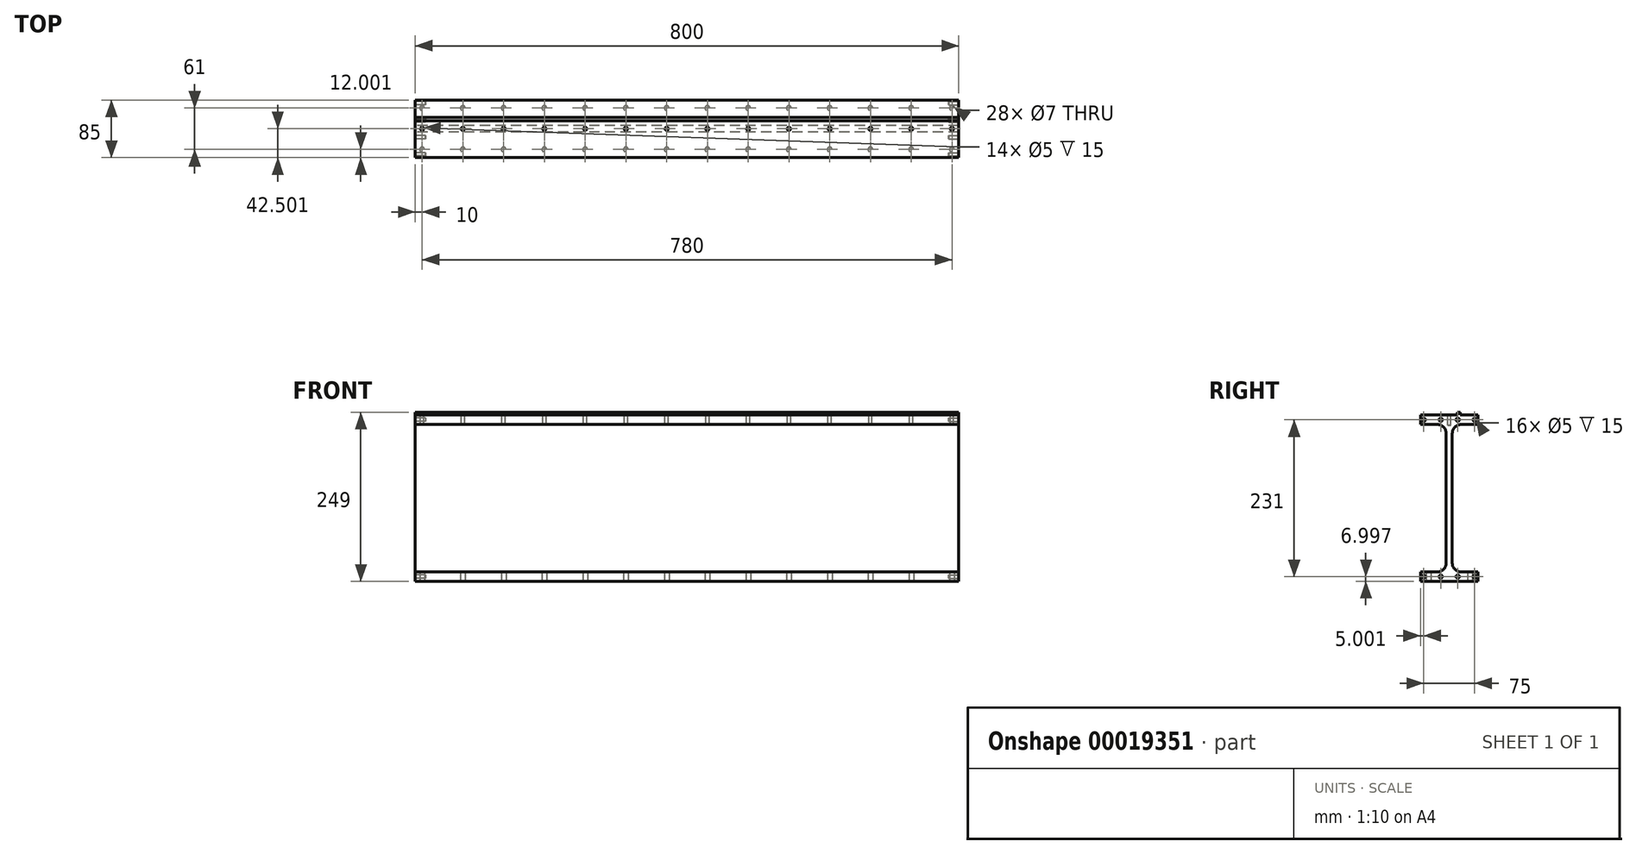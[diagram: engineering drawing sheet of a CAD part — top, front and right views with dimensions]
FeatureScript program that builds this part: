
annotation { "Feature Type Name" : "Feature", "Feature Type Description" : "" }
export const myFeature = defineFeature(function(context is Context, id is Id, definition is map)
    precondition{}
    {
        {
            var Q0;
            Q0=qCreatedBy(makeId("Right.planeOp"),FACE);
            var sketch = newSketch(context, id + "F0", { "sketchPlane" : qUnion([Q0])});
            skLineSegment(sketch, "E0", {"start": v(-399.15, 62.6) * mm, "end": v(-484.15, 62.6) * mm});
            skLineSegment(sketch, "E1", {"start": v(-484.15, 62.6) * mm, "end": v(-484.15, 48.6) * mm});
            skLineSegment(sketch, "E2", {"start": v(-484.15, 48.6) * mm, "end": v(-459.15, 48.6) * mm});
            skLineSegment(sketch, "E3", {"start": v(-446.15, 35.6) * mm, "end": v(-446.15, -155.4) * mm});
            skLineSegment(sketch, "E4", {"start": v(-459.15, -168.4) * mm, "end": v(-484.15, -168.4) * mm});
            skLineSegment(sketch, "E5", {"start": v(-484.15, -168.4) * mm, "end": v(-484.15, -182.4) * mm});
            skLineSegment(sketch, "E6", {"start": v(-484.15, -182.4) * mm, "end": v(-399.15, -182.4) * mm});
            skLineSegment(sketch, "E7", {"start": v(-399.15, -182.4) * mm, "end": v(-399.15, -168.4) * mm});
            skLineSegment(sketch, "E8", {"start": v(-399.15, -168.4) * mm, "end": v(-424.15, -168.4) * mm});
            skLineSegment(sketch, "E9", {"start": v(-437.15, -155.4) * mm, "end": v(-437.15, 35.6) * mm});
            skLineSegment(sketch, "E10", {"start": v(-424.15, 48.6) * mm, "end": v(-399.15, 48.6) * mm});
            skLineSegment(sketch, "E11", {"start": v(-399.15, 48.6) * mm, "end": v(-399.15, 62.6) * mm});
            skArc(sketch, "E12.filletArc", {"start": v(-446.15, 35.6) * mm, "mid": v(-449.96, 44.8) * mm, "end": v(-459.15, 48.6) * mm});
            skArc(sketch, "E13.filletArc", {"start": v(-424.15, 48.6) * mm, "mid": v(-433.34, 44.8) * mm, "end": v(-437.15, 35.6) * mm});
            skArc(sketch, "E14.filletArc", {"start": v(-437.15, -155.4) * mm, "mid": v(-433.34, -164.59) * mm, "end": v(-424.15, -168.4) * mm});
            skArc(sketch, "E15.filletArc", {"start": v(-459.15, -168.4) * mm, "mid": v(-449.96, -164.59) * mm, "end": v(-446.15, -155.4) * mm});
            skSolve(sketch);
        }
        {
            var Q0;
            Q0=makeQuery(id+"F0.imprint","IMPRINT",FACE,{"disambiguationData":[TD([[makeQuery(id+"F0.imprint","IMPRINT",EDGE,{"derivedFrom":sQuery(id+"F0.wireOp",EDGE,"E0")}),1.0]])]});
            extrude(context, id + "F1", {"entities" : qUnion([Q0]), "depth" : 800 * mm});
        }
        {
            var Q0;
            Q0=makeQuery(id+"F1.opExtrude","SWEPT_FACE",FACE,{"disambiguationData":[OSD([sQuery(id+"F0.wireOp",EDGE,"E0")])]});
            var sketch = newSketch(context, id + "F2", { "sketchPlane" : qUnion([Q0])});
            skCircle(sketch, "E16", {"center": v(190, -441.65) * mm, "radius": 2.5 * mm});
            skCircle(sketch, "E17", {"center": v(250, -441.65) * mm, "radius": 2.5 * mm});
            skCircle(sketch, "E18", {"center": v(310, -441.65) * mm, "radius": 2.5 * mm});
            skCircle(sketch, "E19", {"center": v(370, -441.65) * mm, "radius": 2.5 * mm});
            skCircle(sketch, "E20", {"center": v(430, -441.65) * mm, "radius": 2.5 * mm});
            skCircle(sketch, "E21", {"center": v(490, -441.65) * mm, "radius": 2.5 * mm});
            skCircle(sketch, "E22", {"center": v(550, -441.65) * mm, "radius": 2.5 * mm});
            skCircle(sketch, "E23", {"center": v(610, -441.65) * mm, "radius": 2.5 * mm});
            skCircle(sketch, "E24", {"center": v(670, -441.65) * mm, "radius": 2.5 * mm});
            skCircle(sketch, "E25", {"center": v(10, -441.65) * mm, "radius": 2.5 * mm});
            skCircle(sketch, "E26", {"center": v(70, -441.65) * mm, "radius": 2.5 * mm});
            skCircle(sketch, "E27", {"center": v(130, -441.65) * mm, "radius": 2.5 * mm});
            skCircle(sketch, "E28", {"center": v(730, -441.65) * mm, "radius": 2.5 * mm});
            skCircle(sketch, "E29", {"center": v(790, -441.65) * mm, "radius": 2.5 * mm});
            skPoint(sketch, "E30", {"position": v(0, -441.65) * mm});
            skLineSegment(sketch, "E31.bottom", {"start": v(0, -425.15) * mm, "end": v(800, -425.15) * mm});
            skLineSegment(sketch, "E31.top", {"start": v(0, -430.15) * mm, "end": v(800, -430.15) * mm});
            skLineSegment(sketch, "E31.left", {"start": v(0, -425.15) * mm, "end": v(0, -430.15) * mm});
            skLineSegment(sketch, "E31.right", {"start": v(800, -425.15) * mm, "end": v(800, -430.15) * mm});
            skSolve(sketch);
        }
        {
            var Q0;
            Q0=makeQuery(id+"F2.imprint","IMPRINT",FACE,{"disambiguationData":[TD([[makeQuery(id+"F2.imprint","IMPRINT",EDGE,{"derivedFrom":sQuery(id+"F2.wireOp",EDGE,"E25")}),1.0]])]});
            var Q1;
            Q1=makeQuery(id+"F2.imprint","IMPRINT",FACE,{"disambiguationData":[TD([[makeQuery(id+"F2.imprint","IMPRINT",EDGE,{"derivedFrom":sQuery(id+"F2.wireOp",EDGE,"E26")}),1.0]])]});
            var Q2;
            Q2=makeQuery(id+"F2.imprint","IMPRINT",FACE,{"disambiguationData":[TD([[makeQuery(id+"F2.imprint","IMPRINT",EDGE,{"derivedFrom":sQuery(id+"F2.wireOp",EDGE,"E27")}),1.0]])]});
            var Q3;
            Q3=makeQuery(id+"F2.imprint","IMPRINT",FACE,{"disambiguationData":[TD([[makeQuery(id+"F2.imprint","IMPRINT",EDGE,{"derivedFrom":sQuery(id+"F2.wireOp",EDGE,"E16")}),1.0]])]});
            var Q4;
            Q4=makeQuery(id+"F2.imprint","IMPRINT",FACE,{"disambiguationData":[TD([[makeQuery(id+"F2.imprint","IMPRINT",EDGE,{"derivedFrom":sQuery(id+"F2.wireOp",EDGE,"E17")}),1.0]])]});
            var Q5;
            Q5=makeQuery(id+"F2.imprint","IMPRINT",FACE,{"disambiguationData":[TD([[makeQuery(id+"F2.imprint","IMPRINT",EDGE,{"derivedFrom":sQuery(id+"F2.wireOp",EDGE,"E18")}),1.0]])]});
            var Q6;
            Q6=makeQuery(id+"F2.imprint","IMPRINT",FACE,{"disambiguationData":[TD([[makeQuery(id+"F2.imprint","IMPRINT",EDGE,{"derivedFrom":sQuery(id+"F2.wireOp",EDGE,"E19")}),1.0]])]});
            var Q7;
            Q7=makeQuery(id+"F2.imprint","IMPRINT",FACE,{"disambiguationData":[TD([[makeQuery(id+"F2.imprint","IMPRINT",EDGE,{"derivedFrom":sQuery(id+"F2.wireOp",EDGE,"E20")}),1.0]])]});
            var Q8;
            Q8=makeQuery(id+"F2.imprint","IMPRINT",FACE,{"disambiguationData":[TD([[makeQuery(id+"F2.imprint","IMPRINT",EDGE,{"derivedFrom":sQuery(id+"F2.wireOp",EDGE,"E21")}),1.0]])]});
            var Q9;
            Q9=makeQuery(id+"F2.imprint","IMPRINT",FACE,{"disambiguationData":[TD([[makeQuery(id+"F2.imprint","IMPRINT",EDGE,{"derivedFrom":sQuery(id+"F2.wireOp",EDGE,"E22")}),1.0]])]});
            var Q10;
            Q10=makeQuery(id+"F2.imprint","IMPRINT",FACE,{"disambiguationData":[TD([[makeQuery(id+"F2.imprint","IMPRINT",EDGE,{"derivedFrom":sQuery(id+"F2.wireOp",EDGE,"E23")}),1.0]])]});
            var Q11;
            Q11=makeQuery(id+"F2.imprint","IMPRINT",FACE,{"disambiguationData":[TD([[makeQuery(id+"F2.imprint","IMPRINT",EDGE,{"derivedFrom":sQuery(id+"F2.wireOp",EDGE,"E24")}),1.0]])]});
            var Q12;
            Q12=makeQuery(id+"F2.imprint","IMPRINT",FACE,{"disambiguationData":[TD([[makeQuery(id+"F2.imprint","IMPRINT",EDGE,{"derivedFrom":sQuery(id+"F2.wireOp",EDGE,"E28")}),1.0]])]});
            var Q13;
            Q13=makeQuery(id+"F2.imprint","IMPRINT",FACE,{"disambiguationData":[TD([[makeQuery(id+"F2.imprint","IMPRINT",EDGE,{"derivedFrom":sQuery(id+"F2.wireOp",EDGE,"E29")}),1.0]])]});
            extrude(context, id + "F3", {"entities" : qUnion([Q0, Q1, Q2, Q3, Q4, Q5, Q6, Q7, Q8, Q9, Q10, Q11, Q12, Q13]), "operationType" : NewBodyOperationType.REMOVE, "oppositeDirection" : true, "depth" : 15 * mm});
        }
        {
            var Q0;
            Q0=makeQuery(id+"F2.imprint","IMPRINT",FACE,{"disambiguationData":[TD([[makeQuery(id+"F2.imprint","IMPRINT",EDGE,{"derivedFrom":sQuery(id+"F2.wireOp",EDGE,"E31.bottom")}),-1.0]])]});
            extrude(context, id + "F4", {"entities" : qUnion([Q0]), "operationType" : NewBodyOperationType.ADD, "depth" : 4 * mm});
        }
        {
            var Q0;
            Q0=makeQuery(id+"F4.boolean.opBoolean","MERGE",FACE,{"derivedFrom":[makeQuery(id+"F1.opExtrude","CAP_FACE",FACE,{"disambiguationData":[OSD([sQuery(id+"F0.wireOp",EDGE,"E0"),sQuery(id+"F0.wireOp",EDGE,"E1"),sQuery(id+"F0.wireOp",EDGE,"E2"),sQuery(id+"F0.wireOp",EDGE,"E3"),sQuery(id+"F0.wireOp",EDGE,"E4"),sQuery(id+"F0.wireOp",EDGE,"E5"),sQuery(id+"F0.wireOp",EDGE,"E6"),sQuery(id+"F0.wireOp",EDGE,"E7"),sQuery(id+"F0.wireOp",EDGE,"E8"),sQuery(id+"F0.wireOp",EDGE,"E9"),sQuery(id+"F0.wireOp",EDGE,"E10"),sQuery(id+"F0.wireOp",EDGE,"E11"),sQuery(id+"F0.wireOp",EDGE,"E12.filletArc"),sQuery(id+"F0.wireOp",EDGE,"E13.filletArc"),sQuery(id+"F0.wireOp",EDGE,"E14.filletArc"),sQuery(id+"F0.wireOp",EDGE,"E15.filletArc")])],"isStart":true}),makeQuery(id+"F4.opExtrude","SWEPT_FACE",FACE,{"disambiguationData":[OSD([sQuery(id+"F2.wireOp",EDGE,"E31.left")])]})]});
            var sketch = newSketch(context, id + "F5", { "sketchPlane" : qUnion([Q0])});
            skPoint(sketch, "E32", {"position": v(399.15, 55.6) * mm});
            skCircle(sketch, "E33", {"center": v(404.15, 55.6) * mm, "radius": 2.5 * mm});
            skCircle(sketch, "E34", {"center": v(429.15, 55.6) * mm, "radius": 2.5 * mm});
            skCircle(sketch, "E35", {"center": v(454.15, 55.6) * mm, "radius": 2.5 * mm});
            skCircle(sketch, "E36", {"center": v(479.15, 55.6) * mm, "radius": 2.5 * mm});
            skCircle(sketch, "E37", {"center": v(404.15, -175.4) * mm, "radius": 2.5 * mm});
            skCircle(sketch, "E38", {"center": v(429.15, -175.4) * mm, "radius": 2.5 * mm});
            skCircle(sketch, "E39", {"center": v(454.15, -175.4) * mm, "radius": 2.5 * mm});
            skCircle(sketch, "E40", {"center": v(479.15, -175.4) * mm, "radius": 2.5 * mm});
            skPoint(sketch, "E41", {"position": v(399.15, -175.4) * mm});
            skSolve(sketch);
        }
        {
            var Q0;
            Q0=makeQuery(id+"F5.imprint","IMPRINT",FACE,{"disambiguationData":[TD([[makeQuery(id+"F5.imprint","IMPRINT",EDGE,{"derivedFrom":sQuery(id+"F5.wireOp",EDGE,"E33")}),1.0]])]});
            var Q1;
            Q1=makeQuery(id+"F5.imprint","IMPRINT",FACE,{"disambiguationData":[TD([[makeQuery(id+"F5.imprint","IMPRINT",EDGE,{"derivedFrom":sQuery(id+"F5.wireOp",EDGE,"E34")}),1.0]])]});
            var Q2;
            Q2=makeQuery(id+"F5.imprint","IMPRINT",FACE,{"disambiguationData":[TD([[makeQuery(id+"F5.imprint","IMPRINT",EDGE,{"derivedFrom":sQuery(id+"F5.wireOp",EDGE,"E35")}),1.0]])]});
            var Q3;
            Q3=makeQuery(id+"F5.imprint","IMPRINT",FACE,{"disambiguationData":[TD([[makeQuery(id+"F5.imprint","IMPRINT",EDGE,{"derivedFrom":sQuery(id+"F5.wireOp",EDGE,"E36")}),1.0]])]});
            var Q4;
            Q4=makeQuery(id+"F5.imprint","IMPRINT",FACE,{"disambiguationData":[TD([[makeQuery(id+"F5.imprint","IMPRINT",EDGE,{"derivedFrom":sQuery(id+"F5.wireOp",EDGE,"E37")}),1.0]])]});
            var Q5;
            Q5=makeQuery(id+"F5.imprint","IMPRINT",FACE,{"disambiguationData":[TD([[makeQuery(id+"F5.imprint","IMPRINT",EDGE,{"derivedFrom":sQuery(id+"F5.wireOp",EDGE,"E38")}),1.0]])]});
            var Q6;
            Q6=makeQuery(id+"F5.imprint","IMPRINT",FACE,{"disambiguationData":[TD([[makeQuery(id+"F5.imprint","IMPRINT",EDGE,{"derivedFrom":sQuery(id+"F5.wireOp",EDGE,"E39")}),1.0]])]});
            var Q7;
            Q7=makeQuery(id+"F5.imprint","IMPRINT",FACE,{"disambiguationData":[TD([[makeQuery(id+"F5.imprint","IMPRINT",EDGE,{"derivedFrom":sQuery(id+"F5.wireOp",EDGE,"E40")}),1.0]])]});
            extrude(context, id + "F6", {"entities" : qUnion([Q0, Q1, Q2, Q3, Q4, Q5, Q6, Q7]), "operationType" : NewBodyOperationType.REMOVE, "oppositeDirection" : true, "depth" : 15 * mm});
        }
        {
            var Q0;
            Q0=makeQuery(id+"F4.boolean.opBoolean","MERGE",FACE,{"derivedFrom":[makeQuery(id+"F1.opExtrude","CAP_FACE",FACE,{"disambiguationData":[OSD([sQuery(id+"F0.wireOp",EDGE,"E0"),sQuery(id+"F0.wireOp",EDGE,"E1"),sQuery(id+"F0.wireOp",EDGE,"E2"),sQuery(id+"F0.wireOp",EDGE,"E3"),sQuery(id+"F0.wireOp",EDGE,"E4"),sQuery(id+"F0.wireOp",EDGE,"E5"),sQuery(id+"F0.wireOp",EDGE,"E6"),sQuery(id+"F0.wireOp",EDGE,"E7"),sQuery(id+"F0.wireOp",EDGE,"E8"),sQuery(id+"F0.wireOp",EDGE,"E9"),sQuery(id+"F0.wireOp",EDGE,"E10"),sQuery(id+"F0.wireOp",EDGE,"E11"),sQuery(id+"F0.wireOp",EDGE,"E12.filletArc"),sQuery(id+"F0.wireOp",EDGE,"E13.filletArc"),sQuery(id+"F0.wireOp",EDGE,"E14.filletArc"),sQuery(id+"F0.wireOp",EDGE,"E15.filletArc")])],"isStart":false}),makeQuery(id+"F4.opExtrude","SWEPT_FACE",FACE,{"disambiguationData":[OSD([sQuery(id+"F2.wireOp",EDGE,"E31.right")])]})]});
            var sketch = newSketch(context, id + "F7", { "sketchPlane" : qUnion([Q0])});
            skCircle(sketch, "E42", {"center": v(-479.15, -175.4) * mm, "radius": 2.5 * mm});
            skCircle(sketch, "E43", {"center": v(-454.15, -175.4) * mm, "radius": 2.5 * mm});
            skCircle(sketch, "E44", {"center": v(-429.15, -175.4) * mm, "radius": 2.5 * mm});
            skCircle(sketch, "E45", {"center": v(-404.15, -175.4) * mm, "radius": 2.5 * mm});
            skCircle(sketch, "E46", {"center": v(-479.15, 55.6) * mm, "radius": 2.5 * mm});
            skCircle(sketch, "E47", {"center": v(-454.15, 55.6) * mm, "radius": 2.5 * mm});
            skCircle(sketch, "E48", {"center": v(-429.15, 55.6) * mm, "radius": 2.5 * mm});
            skCircle(sketch, "E49", {"center": v(-404.15, 55.6) * mm, "radius": 2.5 * mm});
            skPoint(sketch, "E50", {"position": v(-484.15, 55.6) * mm});
            skPoint(sketch, "E51", {"position": v(-484.15, -175.4) * mm});
            skSolve(sketch);
        }
        {
            var Q0;
            Q0=makeQuery(id+"F7.imprint","IMPRINT",FACE,{"disambiguationData":[TD([[makeQuery(id+"F7.imprint","IMPRINT",EDGE,{"derivedFrom":sQuery(id+"F7.wireOp",EDGE,"E42")}),1.0]])]});
            var Q1;
            Q1=makeQuery(id+"F7.imprint","IMPRINT",FACE,{"disambiguationData":[TD([[makeQuery(id+"F7.imprint","IMPRINT",EDGE,{"derivedFrom":sQuery(id+"F7.wireOp",EDGE,"E43")}),1.0]])]});
            var Q2;
            Q2=makeQuery(id+"F7.imprint","IMPRINT",FACE,{"disambiguationData":[TD([[makeQuery(id+"F7.imprint","IMPRINT",EDGE,{"derivedFrom":sQuery(id+"F7.wireOp",EDGE,"E44")}),1.0]])]});
            var Q3;
            Q3=makeQuery(id+"F7.imprint","IMPRINT",FACE,{"disambiguationData":[TD([[makeQuery(id+"F7.imprint","IMPRINT",EDGE,{"derivedFrom":sQuery(id+"F7.wireOp",EDGE,"E45")}),1.0]])]});
            var Q4;
            Q4=makeQuery(id+"F7.imprint","IMPRINT",FACE,{"disambiguationData":[TD([[makeQuery(id+"F7.imprint","IMPRINT",EDGE,{"derivedFrom":sQuery(id+"F7.wireOp",EDGE,"E46")}),1.0]])]});
            var Q5;
            Q5=makeQuery(id+"F7.imprint","IMPRINT",FACE,{"disambiguationData":[TD([[makeQuery(id+"F7.imprint","IMPRINT",EDGE,{"derivedFrom":sQuery(id+"F7.wireOp",EDGE,"E47")}),1.0]])]});
            var Q6;
            Q6=makeQuery(id+"F7.imprint","IMPRINT",FACE,{"disambiguationData":[TD([[makeQuery(id+"F7.imprint","IMPRINT",EDGE,{"derivedFrom":sQuery(id+"F7.wireOp",EDGE,"E48")}),1.0]])]});
            var Q7;
            Q7=makeQuery(id+"F7.imprint","IMPRINT",FACE,{"disambiguationData":[TD([[makeQuery(id+"F7.imprint","IMPRINT",EDGE,{"derivedFrom":sQuery(id+"F7.wireOp",EDGE,"E49")}),1.0]])]});
            extrude(context, id + "F8", {"entities" : qUnion([Q0, Q1, Q2, Q3, Q4, Q5, Q6, Q7]), "operationType" : NewBodyOperationType.REMOVE, "oppositeDirection" : true, "depth" : 15 * mm});
        }
        {
            var Q0;
            Q0=makeQuery(id+"F1.opExtrude","SWEPT_FACE",FACE,{"disambiguationData":[OSD([sQuery(id+"F0.wireOp",EDGE,"E6")])]});
            var sketch = newSketch(context, id + "F9", { "sketchPlane" : qUnion([Q0])});
            skCircle(sketch, "E52", {"center": v(10, 472.15) * mm, "radius": 3.5 * mm});
            skCircle(sketch, "E53", {"center": v(70, 472.15) * mm, "radius": 3.5 * mm});
            skCircle(sketch, "E54", {"center": v(130, 472.15) * mm, "radius": 3.5 * mm});
            skCircle(sketch, "E55", {"center": v(190, 472.15) * mm, "radius": 3.5 * mm});
            skCircle(sketch, "E56", {"center": v(250, 472.15) * mm, "radius": 3.5 * mm});
            skCircle(sketch, "E57", {"center": v(310, 472.15) * mm, "radius": 3.5 * mm});
            skCircle(sketch, "E58", {"center": v(370, 472.15) * mm, "radius": 3.5 * mm});
            skCircle(sketch, "E59", {"center": v(430, 472.15) * mm, "radius": 3.5 * mm});
            skCircle(sketch, "E60", {"center": v(490, 472.15) * mm, "radius": 3.5 * mm});
            skCircle(sketch, "E61", {"center": v(550, 472.15) * mm, "radius": 3.5 * mm});
            skCircle(sketch, "E62", {"center": v(610, 472.15) * mm, "radius": 3.5 * mm});
            skCircle(sketch, "E63", {"center": v(670, 472.15) * mm, "radius": 3.5 * mm});
            skCircle(sketch, "E64", {"center": v(730, 472.15) * mm, "radius": 3.5 * mm});
            skCircle(sketch, "E65", {"center": v(790, 472.15) * mm, "radius": 3.5 * mm});
            skCircle(sketch, "E66", {"center": v(10, 411.15) * mm, "radius": 3.5 * mm});
            skCircle(sketch, "E67", {"center": v(70, 411.15) * mm, "radius": 3.5 * mm});
            skCircle(sketch, "E68", {"center": v(130, 411.15) * mm, "radius": 3.5 * mm});
            skCircle(sketch, "E69", {"center": v(190, 411.15) * mm, "radius": 3.5 * mm});
            skCircle(sketch, "E70", {"center": v(250, 411.15) * mm, "radius": 3.5 * mm});
            skCircle(sketch, "E71", {"center": v(310, 411.15) * mm, "radius": 3.5 * mm});
            skCircle(sketch, "E72", {"center": v(370, 411.15) * mm, "radius": 3.5 * mm});
            skCircle(sketch, "E73", {"center": v(430, 411.15) * mm, "radius": 3.5 * mm});
            skCircle(sketch, "E74", {"center": v(490, 411.15) * mm, "radius": 3.5 * mm});
            skCircle(sketch, "E75", {"center": v(550, 411.15) * mm, "radius": 3.5 * mm});
            skCircle(sketch, "E76", {"center": v(610, 411.15) * mm, "radius": 3.5 * mm});
            skCircle(sketch, "E77", {"center": v(670, 411.15) * mm, "radius": 3.5 * mm});
            skCircle(sketch, "E78", {"center": v(730, 411.15) * mm, "radius": 3.5 * mm});
            skCircle(sketch, "E79", {"center": v(790, 411.15) * mm, "radius": 3.5 * mm});
            skSolve(sketch);
        }
        {
            var Q0;
            Q0=makeQuery(id+"F9.imprint","IMPRINT",FACE,{"disambiguationData":[TD([[makeQuery(id+"F9.imprint","IMPRINT",EDGE,{"derivedFrom":sQuery(id+"F9.wireOp",EDGE,"E52")}),1.0]])]});
            var Q1;
            Q1=makeQuery(id+"F9.imprint","IMPRINT",FACE,{"disambiguationData":[TD([[makeQuery(id+"F9.imprint","IMPRINT",EDGE,{"derivedFrom":sQuery(id+"F9.wireOp",EDGE,"E66")}),1.0]])]});
            var Q2;
            Q2=makeQuery(id+"F9.imprint","IMPRINT",FACE,{"disambiguationData":[TD([[makeQuery(id+"F9.imprint","IMPRINT",EDGE,{"derivedFrom":sQuery(id+"F9.wireOp",EDGE,"E67")}),1.0]])]});
            var Q3;
            Q3=makeQuery(id+"F9.imprint","IMPRINT",FACE,{"disambiguationData":[TD([[makeQuery(id+"F9.imprint","IMPRINT",EDGE,{"derivedFrom":sQuery(id+"F9.wireOp",EDGE,"E53")}),1.0]])]});
            var Q4;
            Q4=makeQuery(id+"F9.imprint","IMPRINT",FACE,{"disambiguationData":[TD([[makeQuery(id+"F9.imprint","IMPRINT",EDGE,{"derivedFrom":sQuery(id+"F9.wireOp",EDGE,"E54")}),1.0]])]});
            var Q5;
            Q5=makeQuery(id+"F9.imprint","IMPRINT",FACE,{"disambiguationData":[TD([[makeQuery(id+"F9.imprint","IMPRINT",EDGE,{"derivedFrom":sQuery(id+"F9.wireOp",EDGE,"E68")}),1.0]])]});
            var Q6;
            Q6=makeQuery(id+"F9.imprint","IMPRINT",FACE,{"disambiguationData":[TD([[makeQuery(id+"F9.imprint","IMPRINT",EDGE,{"derivedFrom":sQuery(id+"F9.wireOp",EDGE,"E55")}),1.0]])]});
            var Q7;
            Q7=makeQuery(id+"F9.imprint","IMPRINT",FACE,{"disambiguationData":[TD([[makeQuery(id+"F9.imprint","IMPRINT",EDGE,{"derivedFrom":sQuery(id+"F9.wireOp",EDGE,"E69")}),1.0]])]});
            var Q8;
            Q8=makeQuery(id+"F9.imprint","IMPRINT",FACE,{"disambiguationData":[TD([[makeQuery(id+"F9.imprint","IMPRINT",EDGE,{"derivedFrom":sQuery(id+"F9.wireOp",EDGE,"E56")}),1.0]])]});
            var Q9;
            Q9=makeQuery(id+"F9.imprint","IMPRINT",FACE,{"disambiguationData":[TD([[makeQuery(id+"F9.imprint","IMPRINT",EDGE,{"derivedFrom":sQuery(id+"F9.wireOp",EDGE,"E70")}),1.0]])]});
            var Q10;
            Q10=makeQuery(id+"F9.imprint","IMPRINT",FACE,{"disambiguationData":[TD([[makeQuery(id+"F9.imprint","IMPRINT",EDGE,{"derivedFrom":sQuery(id+"F9.wireOp",EDGE,"E57")}),1.0]])]});
            var Q11;
            Q11=makeQuery(id+"F9.imprint","IMPRINT",FACE,{"disambiguationData":[TD([[makeQuery(id+"F9.imprint","IMPRINT",EDGE,{"derivedFrom":sQuery(id+"F9.wireOp",EDGE,"E71")}),1.0]])]});
            var Q12;
            Q12=makeQuery(id+"F9.imprint","IMPRINT",FACE,{"disambiguationData":[TD([[makeQuery(id+"F9.imprint","IMPRINT",EDGE,{"derivedFrom":sQuery(id+"F9.wireOp",EDGE,"E58")}),1.0]])]});
            var Q13;
            Q13=makeQuery(id+"F9.imprint","IMPRINT",FACE,{"disambiguationData":[TD([[makeQuery(id+"F9.imprint","IMPRINT",EDGE,{"derivedFrom":sQuery(id+"F9.wireOp",EDGE,"E72")}),1.0]])]});
            var Q14;
            Q14=makeQuery(id+"F9.imprint","IMPRINT",FACE,{"disambiguationData":[TD([[makeQuery(id+"F9.imprint","IMPRINT",EDGE,{"derivedFrom":sQuery(id+"F9.wireOp",EDGE,"E59")}),1.0]])]});
            var Q15;
            Q15=makeQuery(id+"F9.imprint","IMPRINT",FACE,{"disambiguationData":[TD([[makeQuery(id+"F9.imprint","IMPRINT",EDGE,{"derivedFrom":sQuery(id+"F9.wireOp",EDGE,"E73")}),1.0]])]});
            var Q16;
            Q16=makeQuery(id+"F9.imprint","IMPRINT",FACE,{"disambiguationData":[TD([[makeQuery(id+"F9.imprint","IMPRINT",EDGE,{"derivedFrom":sQuery(id+"F9.wireOp",EDGE,"E74")}),1.0]])]});
            var Q17;
            Q17=makeQuery(id+"F9.imprint","IMPRINT",FACE,{"disambiguationData":[TD([[makeQuery(id+"F9.imprint","IMPRINT",EDGE,{"derivedFrom":sQuery(id+"F9.wireOp",EDGE,"E60")}),1.0]])]});
            var Q18;
            Q18=makeQuery(id+"F9.imprint","IMPRINT",FACE,{"disambiguationData":[TD([[makeQuery(id+"F9.imprint","IMPRINT",EDGE,{"derivedFrom":sQuery(id+"F9.wireOp",EDGE,"E61")}),1.0]])]});
            var Q19;
            Q19=makeQuery(id+"F9.imprint","IMPRINT",FACE,{"disambiguationData":[TD([[makeQuery(id+"F9.imprint","IMPRINT",EDGE,{"derivedFrom":sQuery(id+"F9.wireOp",EDGE,"E75")}),1.0]])]});
            var Q20;
            Q20=makeQuery(id+"F9.imprint","IMPRINT",FACE,{"disambiguationData":[TD([[makeQuery(id+"F9.imprint","IMPRINT",EDGE,{"derivedFrom":sQuery(id+"F9.wireOp",EDGE,"E62")}),1.0]])]});
            var Q21;
            Q21=makeQuery(id+"F9.imprint","IMPRINT",FACE,{"disambiguationData":[TD([[makeQuery(id+"F9.imprint","IMPRINT",EDGE,{"derivedFrom":sQuery(id+"F9.wireOp",EDGE,"E76")}),1.0]])]});
            var Q22;
            Q22=makeQuery(id+"F9.imprint","IMPRINT",FACE,{"disambiguationData":[TD([[makeQuery(id+"F9.imprint","IMPRINT",EDGE,{"derivedFrom":sQuery(id+"F9.wireOp",EDGE,"E77")}),1.0]])]});
            var Q23;
            Q23=makeQuery(id+"F9.imprint","IMPRINT",FACE,{"disambiguationData":[TD([[makeQuery(id+"F9.imprint","IMPRINT",EDGE,{"derivedFrom":sQuery(id+"F9.wireOp",EDGE,"E63")}),1.0]])]});
            var Q24;
            Q24=makeQuery(id+"F9.imprint","IMPRINT",FACE,{"disambiguationData":[TD([[makeQuery(id+"F9.imprint","IMPRINT",EDGE,{"derivedFrom":sQuery(id+"F9.wireOp",EDGE,"E64")}),1.0]])]});
            var Q25;
            Q25=makeQuery(id+"F9.imprint","IMPRINT",FACE,{"disambiguationData":[TD([[makeQuery(id+"F9.imprint","IMPRINT",EDGE,{"derivedFrom":sQuery(id+"F9.wireOp",EDGE,"E78")}),1.0]])]});
            var Q26;
            Q26=makeQuery(id+"F9.imprint","IMPRINT",FACE,{"disambiguationData":[TD([[makeQuery(id+"F9.imprint","IMPRINT",EDGE,{"derivedFrom":sQuery(id+"F9.wireOp",EDGE,"E65")}),1.0]])]});
            var Q27;
            Q27=makeQuery(id+"F9.imprint","IMPRINT",FACE,{"disambiguationData":[TD([[makeQuery(id+"F9.imprint","IMPRINT",EDGE,{"derivedFrom":sQuery(id+"F9.wireOp",EDGE,"E79")}),1.0]])]});
            extrude(context, id + "F10", {"entities" : qUnion([Q0, Q1, Q2, Q3, Q4, Q5, Q6, Q7, Q8, Q9, Q10, Q11, Q12, Q13, Q14, Q15, Q16, Q17, Q18, Q19, Q20, Q21, Q22, Q23, Q24, Q25, Q26, Q27]), "operationType" : NewBodyOperationType.REMOVE, "oppositeDirection" : true, "depth" : 14 * mm});
        }
    });
